# Revit family: Haworth_JiveTable_RacetrackDiscBase
name_source: partatom
category: Furniture Systems
revit_build: Autodesk Revit 2018 (Build: 20170223_1515(x64)
units: mm (PartAtom-declared; Revit-internal decimal feet)

## family parameters
Always vertical = Yes
Cut with Voids When Loaded = No
OmniClass Number = 23.40.70.14.64.21
OmniClass Title = Systems Furniture
Part Type = Normal
Room Calculation Point = No
Round Connector Dimension = Use Diameter
Shared = No
Work Plane-Based = No

## types (6) — shared parameters
Actual Height = 29"
Assembly Code = E2020200
Custom Size = No
Manufacturer = Haworth, Inc.
Max. Depth = 42"
Max. Width = 96"
Min. Depth = 30"
Min. Width = 60"
Model = Haworth Jive
One Disk = No
Revision Number = 0
Size = Verify Final Dim. w/ Haworth
Standard Depths = 30, 36, 42 in.
Standard Widths = 60, 72, 84, 96 in.
Table Thickness = 1 3/16"
Two Disk = Yes
URL = https://www.haworth.com
URL - Product = http://www.haworth.com
Warranty = http://www.haworth.com

## per-type parameters (varying)
| type | Actual Depth | Actual Width | Base Distance | Depth | Description | Disc Distance | Table Radius | Width |
| 30d 60w 29h | 30" | 60" | 30" | 30" | Haworth Jive Table Racetrack Disc Base - 30d 60w 29h | 11" | 15" | 60" |
| 30d 72w 29h | 30" | 72" | 42" | 30" | Haworth Jive Table Racetrack Disc Base - 30d 72w 29h | 11" | 15" | 72" |
| 36d 72w 29h | 36" | 72" | 36" | 36" | Haworth Jive Table Racetrack Disc Base - 36d 72w 29h | 13 1/2" | 18" | 72" |
| 36d 84w 29h | 36" | 84" | 48" | 36" | Haworth Jive Table Racetrack Disc Base - 36d 84w 29h | 13 1/2" | 18" | 84" |
| 42d 84w 29h | 42" | 84" | 42" | 42" | Haworth Jive Table Racetrack Disc Base - 42d 84w 29h | 13 1/2" | 21" | 84" |
| 42d 96w 29h | 42" | 96" | 54" | 42" | Haworth Jive Table Racetrack Disc Base - 42d 96w 29h | 13 1/2" | 21" | 96" |

## geometry (parser evidence)
native form markers: Sweep x6
no freeform markers — native parametric forms only
